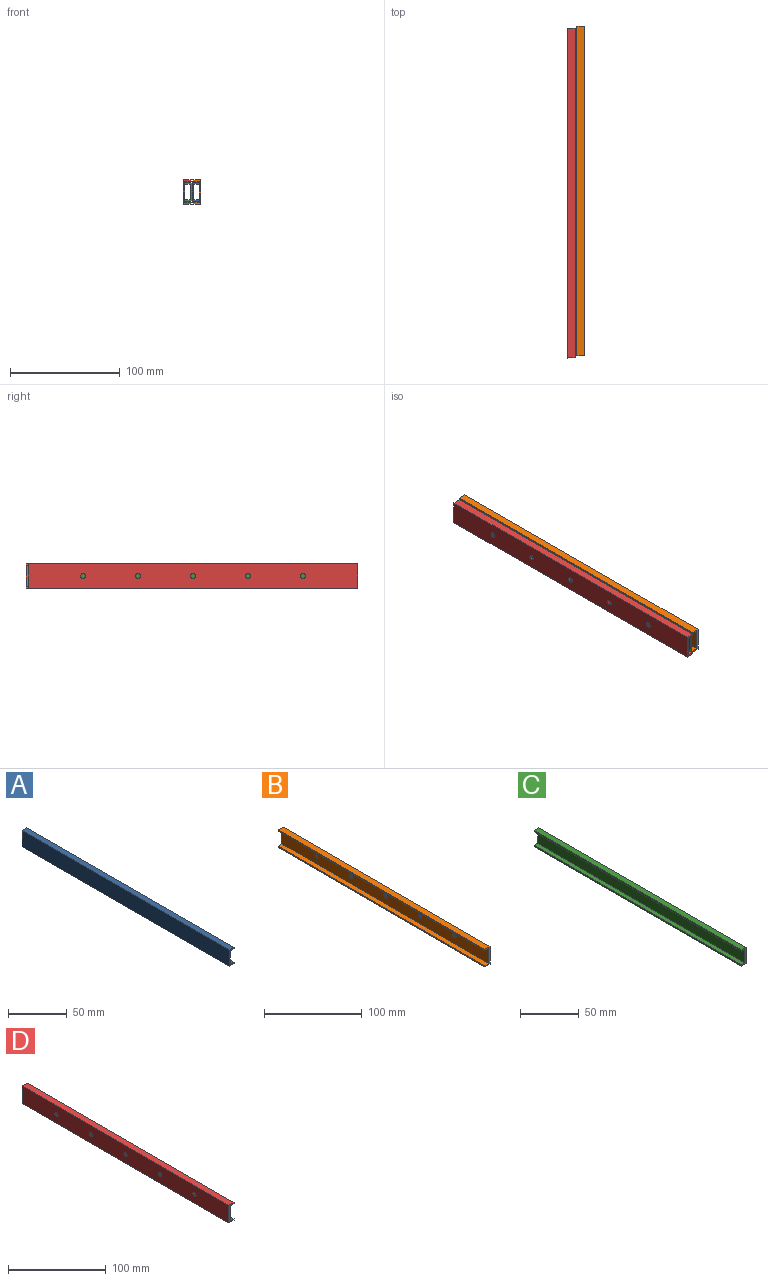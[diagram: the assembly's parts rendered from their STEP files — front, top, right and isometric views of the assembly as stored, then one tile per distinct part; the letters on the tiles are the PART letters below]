
ASSEMBLY  parts=4 mates=3
PART A: 10 faces, bbox 6x250x17 mm
  f0: plane 250x17mm, normal (-1,0,0), area 4250mm2, adj f1,f7,f8,f9
  f1: plane 250x6mm, normal (0,0,-1), area 1500mm2, adj f0,f2,f8,f9
  f2: plane 250x1.5mm, normal (1,0,0), area 375mm2, adj f1,f3,f8,f9
  f3: plane 250x4.5mm, normal (0,0,1), area 1125mm2, adj f2,f4,f8,f9
  f4: plane 250x14mm, normal (1,0,0), area 3500mm2, adj f3,f5,f8,f9
  f5: plane 250x4.5mm, normal (0,0,-1), area 1125mm2, adj f4,f6,f8,f9
  f6: plane 250x1.5mm, normal (1,0,0), area 375mm2, adj f5,f7,f8,f9
  f7: plane 250x6mm, normal (0,0,1), area 1500mm2, adj f0,f6,f8,f9
  f8: plane 17x6mm, normal (0,-1,0), area 39mm2, adj f0,f1,f2,f3,f4,f5,f6,f7
  f9: plane 17x6mm, normal (0,1,0), area 39mm2, adj f0,f1,f2,f3,f4,f5,f6,f7
PART B: 15 faces, bbox 7.3x300x22 mm
  f0: plane 300x19mm, normal (-1,0,0), area 5620.5mm2, adj f3,f4,f8,f9,f10,f11,f12,f13
  f1: plane 300x22mm, normal (1,0,0), area 6520.5mm2, adj f6,f7,f8,f9,f10,f11,f12,f13
  f2: plane 300x1.5mm, normal (-1,0,0), area 450mm2, adj f3,f7,f8,f9
  f3: plane 300x5.75mm, normal (0,0,-1), area 1725mm2, adj f0,f2,f8,f9
  f4: plane 300x5.75mm, normal (0,0,1), area 1725mm2, adj f0,f5,f8,f9
  f5: plane 300x1.5mm, normal (-1,0,0), area 450mm2, adj f4,f6,f8,f9
  f6: plane 300x7.25mm, normal (0,0,-1), area 2175mm2, adj f1,f5,f8,f9
  f7: plane 300x7.25mm, normal (0,0,1), area 2175mm2, adj f1,f2,f8,f9
  f8: plane 22x7.25mm, normal (0,-1,0), area 50.2mm2, adj f0,f1,f2,f3,f4,f5,f6,f7
  f9: plane 22x7.25mm, normal (0,1,0), area 50.2mm2, adj f0,f1,f2,f3,f4,f5,f6,f7
  f10: cylinder r=2.25mm len=4.5mm, axis (1,0,0), area 21.2mm2, adj f0,f1
  f11: cylinder r=2.25mm len=4.5mm, axis (1,0,0), area 21.2mm2, adj f0,f1
  f12: cylinder r=2.25mm len=4.5mm, axis (1,0,0), area 21.2mm2, adj f0,f1
  f13: cylinder r=2.25mm len=4.5mm, axis (1,0,0), area 21.2mm2, adj f0,f1
  f14: cylinder r=2.25mm len=4.5mm, axis (1,0,0), area 21.2mm2, adj f0,f1
PART C: 10 faces, bbox 6x250x17 mm
  f0: plane 250x17mm, normal (1,0,0), area 4250mm2, adj f1,f7,f8,f9
  f1: plane 250x6mm, normal (0,0,1), area 1500mm2, adj f0,f2,f8,f9
  f2: plane 250x1.5mm, normal (-1,0,0), area 375mm2, adj f1,f3,f8,f9
  f3: plane 250x4.5mm, normal (0,0,-1), area 1125mm2, adj f2,f4,f8,f9
  f4: plane 250x14mm, normal (-1,0,0), area 3500mm2, adj f3,f5,f8,f9
  f5: plane 250x4.5mm, normal (0,0,1), area 1125mm2, adj f4,f6,f8,f9
  f6: plane 250x1.5mm, normal (-1,0,0), area 375mm2, adj f5,f7,f8,f9
  f7: plane 250x6mm, normal (0,0,-1), area 1500mm2, adj f0,f6,f8,f9
  f8: plane 17x6mm, normal (0,-1,0), area 39mm2, adj f0,f1,f2,f3,f4,f5,f6,f7
  f9: plane 17x6mm, normal (0,1,0), area 39mm2, adj f0,f1,f2,f3,f4,f5,f6,f7
PART D: 15 faces, bbox 7.3x300x22 mm
  f0: plane 300x19mm, normal (1,0,0), area 5620.5mm2, adj f4,f5,f8,f9,f10,f11,f12,f13
  f1: plane 300x22mm, normal (-1,0,0), area 6520.5mm2, adj f2,f7,f8,f9,f10,f11,f12,f13
  f2: plane 300x7.25mm, normal (0,0,-1), area 2175mm2, adj f1,f3,f8,f9
  f3: plane 300x1.5mm, normal (1,0,0), area 450mm2, adj f2,f4,f8,f9
  f4: plane 300x5.75mm, normal (0,0,1), area 1725mm2, adj f0,f3,f8,f9
  f5: plane 300x5.75mm, normal (0,0,-1), area 1725mm2, adj f0,f6,f8,f9
  f6: plane 300x1.5mm, normal (1,0,0), area 450mm2, adj f5,f7,f8,f9
  f7: plane 300x7.25mm, normal (0,0,1), area 2175mm2, adj f1,f6,f8,f9
  f8: plane 22x7.25mm, normal (0,-1,0), area 50.3mm2, adj f0,f1,f2,f3,f4,f5,f6,f7
  f9: plane 22x7.25mm, normal (0,1,0), area 50.3mm2, adj f0,f1,f2,f3,f4,f5,f6,f7
  f10: cylinder r=2.25mm len=4.5mm, axis (1,0,0), area 21.2mm2, adj f0,f1
  f11: cylinder r=2.25mm len=4.5mm, axis (1,0,0), area 21.2mm2, adj f0,f1
  f12: cylinder r=2.25mm len=4.5mm, axis (1,0,0), area 21.2mm2, adj f0,f1
  f13: cylinder r=2.25mm len=4.5mm, axis (1,0,0), area 21.2mm2, adj f0,f1
  f14: cylinder r=2.25mm len=4.5mm, axis (1,0,0), area 21.2mm2, adj f0,f1
PLACE A t=(48.06,-39.63,0.07)mm
PLACE B t=(35.84,-37.63,0.07)mm
PLACE C t=(62.9,-87.63,0.07)mm
PLACE D rot(axis=(0,-1,0),0deg) t=(75.12,-39.63,0.07)mm
MATE fastened A.f0 <-> C.f0  axis (-1,0,0) through (31.21,-164.63,1.84)mm
MATE slider B.f9 <-> A.f9  axis (0,1,0) through (37.71,-37.63,1.84)mm
MATE slider D.f8 <-> C.f8  axis (0,-1,0) through (24.71,-339.63,1.84)mm
